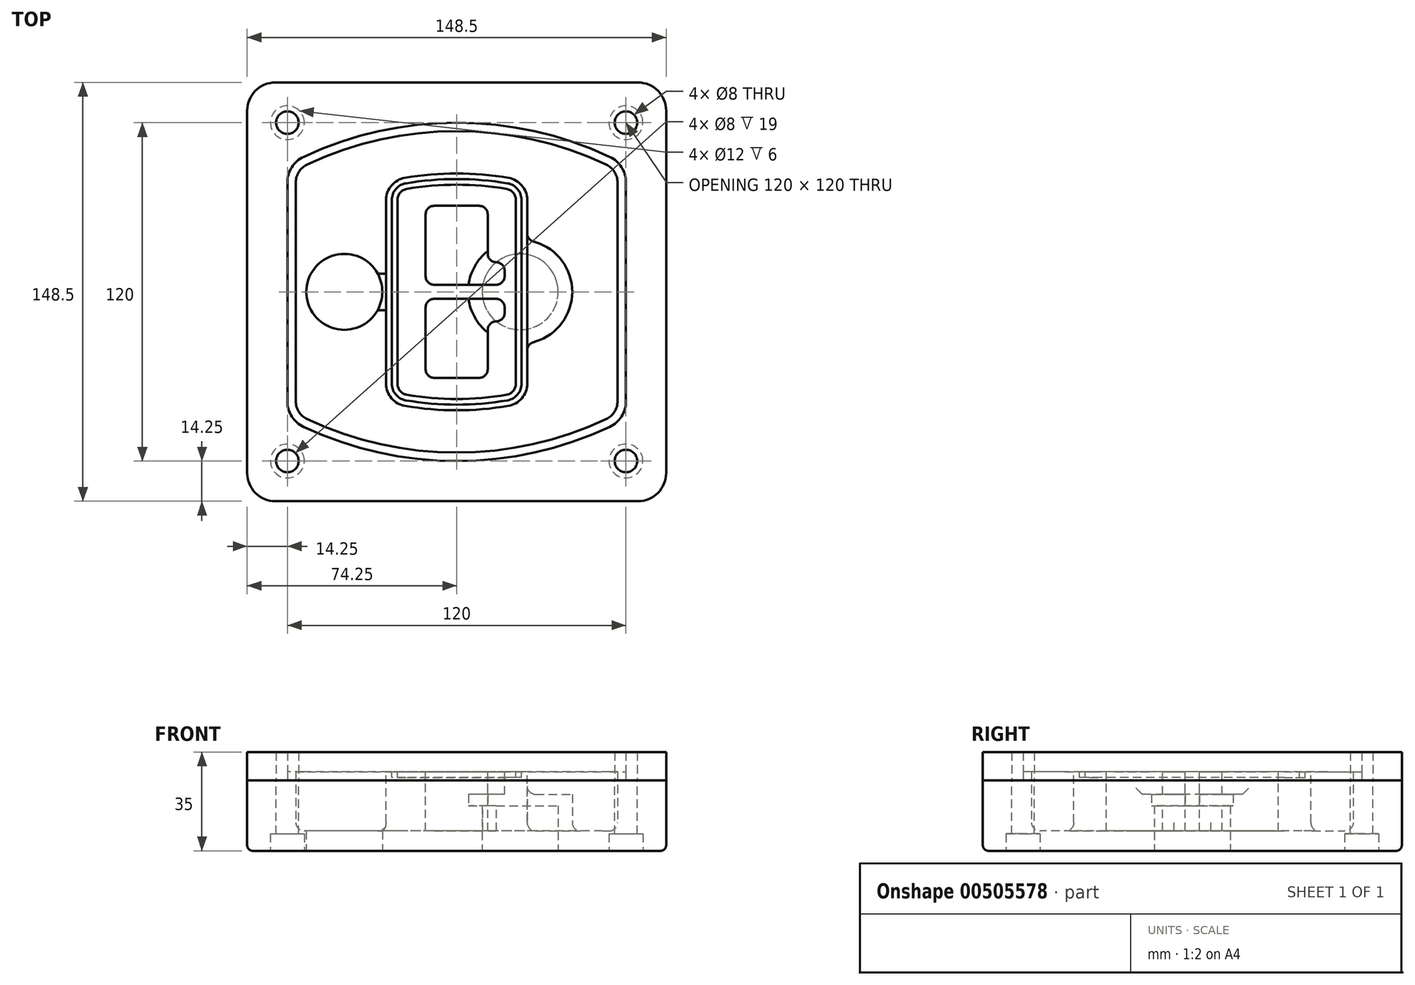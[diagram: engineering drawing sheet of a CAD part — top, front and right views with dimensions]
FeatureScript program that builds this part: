
annotation { "Feature Type Name" : "Feature", "Feature Type Description" : "" }
export const myFeature = defineFeature(function(context is Context, id is Id, definition is map)
    precondition{}
    {
        {
            var Q0;
            Q0=qCreatedBy(makeId("Top.planeOp"),FACE);
            var sketch = newSketch(context, id + "F0", { "sketchPlane" : qUnion([Q0])});
            skPoint(sketch, "E0.rect.middle", {"position": v(0, 0) * mm});
            skLineSegment(sketch, "E1.bottom", {"start": v(-64.25, -74.25) * mm, "end": v(64.25, -74.25) * mm});
            skLineSegment(sketch, "E1.top", {"start": v(-64.25, 74.25) * mm, "end": v(64.25, 74.25) * mm});
            skLineSegment(sketch, "E1.left", {"start": v(-74.25, -64.25) * mm, "end": v(-74.25, 64.25) * mm});
            skLineSegment(sketch, "E1.right", {"start": v(74.25, -64.25) * mm, "end": v(74.25, 64.25) * mm});
            skLineSegment(sketch, "E2", {"start": v(-74.25, 74.25) * mm, "end": v(74.25, -74.25) * mm, "construction": true});
            skLineSegment(sketch, "E3", {"start": v(74.25, 74.25) * mm, "end": v(-74.25, -74.25) * mm, "construction": true});
            skCircle(sketch, "E4", {"center": v(-60, 60) * mm, "radius": 4 * mm});
            skCircle(sketch, "E5", {"center": v(60, 60) * mm, "radius": 4 * mm});
            skCircle(sketch, "E6", {"center": v(60, -60) * mm, "radius": 4 * mm});
            skCircle(sketch, "E7", {"center": v(-60, -60) * mm, "radius": 4 * mm});
            skLineSegment(sketch, "E8", {"start": v(-60, 60) * mm, "end": v(60, 60) * mm, "construction": true});
            skLineSegment(sketch, "E9", {"start": v(60, 60) * mm, "end": v(60, -60) * mm, "construction": true});
            skLineSegment(sketch, "E10", {"start": v(60, -60) * mm, "end": v(-60, -60) * mm, "construction": true});
            skLineSegment(sketch, "E11", {"start": v(-60, -60) * mm, "end": v(-60, 60) * mm, "construction": true});
            skLineSegment(sketch, "E12", {"start": v(-60, 38.83) * mm, "end": v(-60, -38.83) * mm});
            skLineSegment(sketch, "E13", {"start": v(60, 38.83) * mm, "end": v(60, -38.83) * mm});
            skArc(sketch, "E14", {"start": v(54.26, 47.88) * mm, "mid": v(0, 60) * mm, "end": v(-54.26, 47.88) * mm});
            skArc(sketch, "E15", {"start": v(-54.26, -47.88) * mm, "mid": v(0, -60) * mm, "end": v(54.26, -47.88) * mm});
            skLineSegment(sketch, "E16", {"start": v(-60, 0) * mm, "end": v(60, 0) * mm, "construction": true});
            skPoint(sketch, "E17.visualSharp", {"position": v(-60, -45) * mm});
            skArc(sketch, "E17.filletArc", {"start": v(-60, -38.83) * mm, "mid": v(-58.44, -44.2) * mm, "end": v(-54.26, -47.88) * mm});
            skPoint(sketch, "E18.visualSharp", {"position": v(-60, 45) * mm});
            skArc(sketch, "E18.filletArc", {"start": v(-54.26, 47.88) * mm, "mid": v(-58.44, 44.2) * mm, "end": v(-60, 38.83) * mm});
            skPoint(sketch, "E19.visualSharp", {"position": v(60, 45) * mm});
            skArc(sketch, "E19.filletArc", {"start": v(60, 38.83) * mm, "mid": v(58.44, 44.2) * mm, "end": v(54.26, 47.88) * mm});
            skPoint(sketch, "E20.visualSharp", {"position": v(60, -45) * mm});
            skArc(sketch, "E20.filletArc", {"start": v(54.26, -47.88) * mm, "mid": v(58.44, -44.2) * mm, "end": v(60, -38.83) * mm});
            skPoint(sketch, "E21.visualSharp", {"position": v(-74.25, 74.25) * mm});
            skArc(sketch, "E21.filletArc", {"start": v(-64.25, 74.25) * mm, "mid": v(-71.32, 71.32) * mm, "end": v(-74.25, 64.25) * mm});
            skPoint(sketch, "E22.visualSharp", {"position": v(74.25, 74.25) * mm});
            skArc(sketch, "E22.filletArc", {"start": v(74.25, 64.25) * mm, "mid": v(71.32, 71.32) * mm, "end": v(64.25, 74.25) * mm});
            skPoint(sketch, "E23.visualSharp", {"position": v(74.25, -74.25) * mm});
            skArc(sketch, "E23.filletArc", {"start": v(64.25, -74.25) * mm, "mid": v(71.32, -71.32) * mm, "end": v(74.25, -64.25) * mm});
            skPoint(sketch, "E24.visualSharp", {"position": v(-74.25, -74.25) * mm});
            skArc(sketch, "E24.filletArc", {"start": v(-74.25, -64.25) * mm, "mid": v(-71.32, -71.32) * mm, "end": v(-64.25, -74.25) * mm});
            skArc(sketch, "E25.0", {"start": v(57, 38.83) * mm, "mid": v(55.9, 42.58) * mm, "end": v(52.98, 45.17) * mm});
            skLineSegment(sketch, "E25.1", {"start": v(57, 38.83) * mm, "end": v(57, -38.83) * mm});
            skArc(sketch, "E25.2", {"start": v(52.98, -45.17) * mm, "mid": v(55.9, -42.58) * mm, "end": v(57, -38.83) * mm});
            skArc(sketch, "E25.3", {"start": v(-52.98, -45.17) * mm, "mid": v(0, -57) * mm, "end": v(52.98, -45.17) * mm});
            skArc(sketch, "E25.4", {"start": v(-57, -38.83) * mm, "mid": v(-55.9, -42.58) * mm, "end": v(-52.98, -45.17) * mm});
            skArc(sketch, "E25.5", {"start": v(52.98, 45.17) * mm, "mid": v(0, 57) * mm, "end": v(-52.98, 45.17) * mm});
            skLineSegment(sketch, "E25.6", {"start": v(-57, 38.83) * mm, "end": v(-57, -38.83) * mm});
            skArc(sketch, "E25.7", {"start": v(-52.98, 45.17) * mm, "mid": v(-55.9, 42.58) * mm, "end": v(-57, 38.83) * mm});
            skArc(sketch, "E26.0", {"start": v(-55.96, 51.5) * mm, "mid": v(-61.82, 46.33) * mm, "end": v(-64, 38.83) * mm});
            skArc(sketch, "E26.1", {"start": v(55.96, 51.5) * mm, "mid": v(0, 64) * mm, "end": v(-55.96, 51.5) * mm});
            skArc(sketch, "E26.2", {"start": v(64, 38.83) * mm, "mid": v(61.82, 46.33) * mm, "end": v(55.96, 51.5) * mm});
            skLineSegment(sketch, "E26.3", {"start": v(64, 38.83) * mm, "end": v(64, -38.83) * mm});
            skArc(sketch, "E26.4", {"start": v(55.96, -51.5) * mm, "mid": v(61.82, -46.33) * mm, "end": v(64, -38.83) * mm});
            skLineSegment(sketch, "E26.5", {"start": v(-64, 38.83) * mm, "end": v(-64, -38.83) * mm});
            skArc(sketch, "E26.6", {"start": v(-55.96, -51.5) * mm, "mid": v(0, -64) * mm, "end": v(55.96, -51.5) * mm});
            skArc(sketch, "E26.7", {"start": v(-64, -38.83) * mm, "mid": v(-61.82, -46.33) * mm, "end": v(-55.96, -51.5) * mm});
            skSolve(sketch);
        }
        {
            var Q0;
            Q0=makeQuery(id+"F0.imprint","IMPRINT",FACE,{"disambiguationData":[TD([[makeQuery(id+"F0.imprint","IMPRINT",EDGE,{"derivedFrom":sQuery(id+"F0.wireOp",EDGE,"E1.bottom")}),1.0]])]});
            var Q1;
            Q1=makeQuery(id+"F0.imprint","IMPRINT",FACE,{"disambiguationData":[TD([[makeQuery(id+"F0.imprint","IMPRINT",EDGE,{"derivedFrom":sQuery(id+"F0.wireOp",EDGE,"E12")}),1.0]])]});
            var Q2;
            Q2=makeQuery(id+"F0.imprint","IMPRINT",FACE,{"disambiguationData":[TD([[makeQuery(id+"F0.imprint","IMPRINT",EDGE,{"derivedFrom":sQuery(id+"F0.wireOp",EDGE,"E25.0")}),1.0]])]});
            var Q3;
            Q3=makeQuery(id+"F0.imprint","IMPRINT",FACE,{"disambiguationData":[TD([[makeQuery(id+"F0.imprint","IMPRINT",EDGE,{"derivedFrom":sQuery(id+"F0.wireOp",EDGE,"E12")}),-1.0]])]});
            extrude(context, id + "F1", {"entities" : qUnion([Q0, Q1, Q2, Q3]), "oppositeDirection" : true, "depth" : 25 * mm});
        }
        {
            var Q0;
            Q0=makeQuery(id+"F0.imprint","IMPRINT",FACE,{"disambiguationData":[TD([[makeQuery(id+"F0.imprint","IMPRINT",EDGE,{"derivedFrom":sQuery(id+"F0.wireOp",EDGE,"E12")}),1.0]])]});
            extrude(context, id + "F2", {"entities" : qUnion([Q0]), "operationType" : NewBodyOperationType.ADD, "depth" : 3 * mm});
        }
        {
            var Q0;
            Q0=makeQuery(id+"F0.imprint","IMPRINT",FACE,{"disambiguationData":[TD([[makeQuery(id+"F0.imprint","IMPRINT",EDGE,{"derivedFrom":sQuery(id+"F0.wireOp",EDGE,"E25.0")}),1.0]])]});
            extrude(context, id + "F3", {"entities" : qUnion([Q0]), "operationType" : NewBodyOperationType.REMOVE, "oppositeDirection" : true, "depth" : 18 * mm});
        }
        {
            var Q0;
            Q0=makeQuery(id+"F2.opExtrude","CAP_FACE",FACE,{"disambiguationData":[OSD([sQuery(id+"F0.wireOp",EDGE,"E12"),sQuery(id+"F0.wireOp",EDGE,"E13"),sQuery(id+"F0.wireOp",EDGE,"E14"),sQuery(id+"F0.wireOp",EDGE,"E15"),sQuery(id+"F0.wireOp",EDGE,"E17.filletArc"),sQuery(id+"F0.wireOp",EDGE,"E18.filletArc"),sQuery(id+"F0.wireOp",EDGE,"E19.filletArc"),sQuery(id+"F0.wireOp",EDGE,"E20.filletArc"),sQuery(id+"F0.wireOp",EDGE,"E25.0"),sQuery(id+"F0.wireOp",EDGE,"E25.1"),sQuery(id+"F0.wireOp",EDGE,"E25.2"),sQuery(id+"F0.wireOp",EDGE,"E25.3"),sQuery(id+"F0.wireOp",EDGE,"E25.4"),sQuery(id+"F0.wireOp",EDGE,"E25.5"),sQuery(id+"F0.wireOp",EDGE,"E25.6"),sQuery(id+"F0.wireOp",EDGE,"E25.7")])],"isStart":false});
            var sketch = newSketch(context, id + "F4", { "sketchPlane" : qUnion([Q0])});
            skArc(sketch, "E27.0", {"start": v(-18.34, -40.45) * mm, "mid": v(0, -42) * mm, "end": v(18.34, -40.45) * mm});
            skArc(sketch, "E28.0", {"start": v(18.34, 40.45) * mm, "mid": v(0, 42) * mm, "end": v(-18.34, 40.45) * mm});
            skLineSegment(sketch, "E29", {"start": v(-25, 32.57) * mm, "end": v(-25, -32.57) * mm});
            skLineSegment(sketch, "E30", {"start": v(25, 32.57) * mm, "end": v(25, -32.57) * mm});
            skLineSegment(sketch, "E31", {"start": v(-25, 39.1) * mm, "end": v(25, 39.1) * mm, "construction": true});
            skLineSegment(sketch, "E32", {"start": v(-25, -39.1) * mm, "end": v(25, -39.1) * mm, "construction": true});
            skPoint(sketch, "E33.visualSharp", {"position": v(-25, 39.1) * mm});
            skArc(sketch, "E33.filletArc", {"start": v(-18.34, 40.45) * mm, "mid": v(-23.11, 37.73) * mm, "end": v(-25, 32.57) * mm});
            skPoint(sketch, "E34.visualSharp", {"position": v(25, 39.1) * mm});
            skArc(sketch, "E34.filletArc", {"start": v(25, 32.57) * mm, "mid": v(23.11, 37.73) * mm, "end": v(18.34, 40.45) * mm});
            skPoint(sketch, "E35.visualSharp", {"position": v(25, -39.1) * mm});
            skArc(sketch, "E35.filletArc", {"start": v(18.34, -40.45) * mm, "mid": v(23.11, -37.73) * mm, "end": v(25, -32.57) * mm});
            skPoint(sketch, "E36.visualSharp", {"position": v(-25, -39.1) * mm});
            skArc(sketch, "E36.filletArc", {"start": v(-25, -32.57) * mm, "mid": v(-23.11, -37.73) * mm, "end": v(-18.34, -40.45) * mm});
            skArc(sketch, "E37.0", {"start": v(52.98, 45.17) * mm, "mid": v(0, 57) * mm, "end": v(-52.98, 45.17) * mm});
            skArc(sketch, "E37.1", {"start": v(-52.98, 45.17) * mm, "mid": v(-55.9, 42.58) * mm, "end": v(-57, 38.83) * mm});
            skLineSegment(sketch, "E37.2", {"start": v(-57, 38.83) * mm, "end": v(-57, -38.83) * mm});
            skArc(sketch, "E37.3", {"start": v(-57, -38.83) * mm, "mid": v(-55.9, -42.58) * mm, "end": v(-52.98, -45.17) * mm});
            skArc(sketch, "E37.4", {"start": v(-52.98, -45.17) * mm, "mid": v(0, -57) * mm, "end": v(52.98, -45.17) * mm});
            skArc(sketch, "E37.5", {"start": v(52.98, -45.17) * mm, "mid": v(55.9, -42.58) * mm, "end": v(57, -38.83) * mm});
            skLineSegment(sketch, "E37.6", {"start": v(57, 38.83) * mm, "end": v(57, -38.83) * mm});
            skArc(sketch, "E37.7", {"start": v(57, 38.83) * mm, "mid": v(55.9, 42.58) * mm, "end": v(52.98, 45.17) * mm});
            skLineSegment(sketch, "E38.0", {"start": v(23, 32.57) * mm, "end": v(23, -32.57) * mm});
            skArc(sketch, "E38.1", {"start": v(18, -38.48) * mm, "mid": v(21.58, -36.44) * mm, "end": v(23, -32.57) * mm});
            skArc(sketch, "E38.2", {"start": v(-18, -38.48) * mm, "mid": v(0, -40) * mm, "end": v(18, -38.48) * mm});
            skArc(sketch, "E38.3", {"start": v(-23, -32.57) * mm, "mid": v(-21.58, -36.44) * mm, "end": v(-18, -38.48) * mm});
            skLineSegment(sketch, "E38.4", {"start": v(-23, 32.57) * mm, "end": v(-23, -32.57) * mm});
            skArc(sketch, "E38.5", {"start": v(23, 32.57) * mm, "mid": v(21.58, 36.44) * mm, "end": v(18, 38.48) * mm});
            skArc(sketch, "E38.6", {"start": v(-18, 38.48) * mm, "mid": v(-21.58, 36.44) * mm, "end": v(-23, 32.57) * mm});
            skArc(sketch, "E38.7", {"start": v(18, 38.48) * mm, "mid": v(0, 40) * mm, "end": v(-18, 38.48) * mm});
            skArc(sketch, "E39.0", {"start": v(21, 32.57) * mm, "mid": v(20.06, 35.15) * mm, "end": v(17.67, 36.5) * mm});
            skLineSegment(sketch, "E39.1", {"start": v(21, 32.57) * mm, "end": v(21, -32.57) * mm});
            skArc(sketch, "E39.2", {"start": v(17.67, -36.5) * mm, "mid": v(20.06, -35.15) * mm, "end": v(21, -32.57) * mm});
            skArc(sketch, "E39.3", {"start": v(-17.67, -36.5) * mm, "mid": v(0, -38) * mm, "end": v(17.67, -36.5) * mm});
            skArc(sketch, "E39.4", {"start": v(-21, -32.57) * mm, "mid": v(-20.06, -35.15) * mm, "end": v(-17.67, -36.5) * mm});
            skArc(sketch, "E39.5", {"start": v(17.67, 36.5) * mm, "mid": v(0, 38) * mm, "end": v(-17.67, 36.5) * mm});
            skLineSegment(sketch, "E39.6", {"start": v(-21, 32.57) * mm, "end": v(-21, -32.57) * mm});
            skArc(sketch, "E39.7", {"start": v(-17.67, 36.5) * mm, "mid": v(-20.06, 35.15) * mm, "end": v(-21, 32.57) * mm});
            skLineSegment(sketch, "E40", {"start": v(-25, 0) * mm, "end": v(25, 0) * mm, "construction": true});
            skLineSegment(sketch, "E41", {"start": v(-11, 5.5) * mm, "end": v(-11, 27.5) * mm});
            skLineSegment(sketch, "E42", {"start": v(-8, 30.5) * mm, "end": v(8, 30.5) * mm});
            skLineSegment(sketch, "E43", {"start": v(11, 27.5) * mm, "end": v(11, 13.5) * mm});
            skLineSegment(sketch, "E44", {"start": v(14, 10.5) * mm, "end": v(14, 10.5) * mm});
            skLineSegment(sketch, "E45", {"start": v(17, 7.5) * mm, "end": v(17, 5.5) * mm});
            skLineSegment(sketch, "E46", {"start": v(14, 2.5) * mm, "end": v(-8, 2.5) * mm});
            skPoint(sketch, "E47.visualSharp", {"position": v(-11, 30.5) * mm});
            skArc(sketch, "E47.filletArc", {"start": v(-8, 30.5) * mm, "mid": v(-10.12, 29.62) * mm, "end": v(-11, 27.5) * mm});
            skPoint(sketch, "E48.visualSharp", {"position": v(11, 30.5) * mm});
            skArc(sketch, "E48.filletArc", {"start": v(11, 27.5) * mm, "mid": v(10.12, 29.62) * mm, "end": v(8, 30.5) * mm});
            skPoint(sketch, "E49.visualSharp", {"position": v(11, 10.5) * mm});
            skArc(sketch, "E49.filletArc", {"start": v(11, 13.5) * mm, "mid": v(11.88, 11.38) * mm, "end": v(14, 10.5) * mm});
            skPoint(sketch, "E50.visualSharp", {"position": v(17, 10.5) * mm});
            skArc(sketch, "E50.filletArc", {"start": v(17, 7.5) * mm, "mid": v(16.12, 9.62) * mm, "end": v(14, 10.5) * mm});
            skPoint(sketch, "E51.visualSharp", {"position": v(17, 2.5) * mm});
            skArc(sketch, "E51.filletArc", {"start": v(14, 2.5) * mm, "mid": v(16.12, 3.38) * mm, "end": v(17, 5.5) * mm});
            skPoint(sketch, "E52.visualSharp", {"position": v(-11, 2.5) * mm});
            skArc(sketch, "E52.filletArc", {"start": v(-11, 5.5) * mm, "mid": v(-10.12, 3.38) * mm, "end": v(-8, 2.5) * mm});
            skLineSegment(sketch, "E53.0.MirrorCS", {"start": v(14, -2.5) * mm, "end": v(-8, -2.5) * mm});
            skArc(sketch, "E54.0.MirrorCS", {"start": v(-11, -5.5) * mm, "mid": v(-10.12, -3.38) * mm, "end": v(-8, -2.5) * mm});
            skLineSegment(sketch, "E55.0.MirrorCS", {"start": v(-11, -5.5) * mm, "end": v(-11, -27.5) * mm});
            skArc(sketch, "E56.0.MirrorCS", {"start": v(-8, -30.5) * mm, "mid": v(-10.12, -29.62) * mm, "end": v(-11, -27.5) * mm});
            skLineSegment(sketch, "E57.0.MirrorCS", {"start": v(-8, -30.5) * mm, "end": v(8, -30.5) * mm});
            skArc(sketch, "E58.0.MirrorCS", {"start": v(11, -27.5) * mm, "mid": v(10.12, -29.62) * mm, "end": v(8, -30.5) * mm});
            skLineSegment(sketch, "E59.0.MirrorCS", {"start": v(11, -27.5) * mm, "end": v(11, -13.5) * mm});
            skArc(sketch, "E60.0.MirrorCS", {"start": v(11, -13.5) * mm, "mid": v(11.88, -11.38) * mm, "end": v(14, -10.5) * mm});
            skArc(sketch, "E61.0.MirrorCS", {"start": v(17, -7.5) * mm, "mid": v(16.12, -9.62) * mm, "end": v(14, -10.5) * mm});
            skLineSegment(sketch, "E62.0.MirrorCS", {"start": v(17, -7.5) * mm, "end": v(17, -5.5) * mm});
            skArc(sketch, "E63.0.MirrorCS", {"start": v(14, -2.5) * mm, "mid": v(16.12, -3.38) * mm, "end": v(17, -5.5) * mm});
            skSolve(sketch);
        }
        {
            var Q0;
            Q0=makeQuery(id+"F4.imprint","IMPRINT",FACE,{"disambiguationData":[TD([[makeQuery(id+"F4.imprint","IMPRINT",EDGE,{"derivedFrom":sQuery(id+"F4.wireOp",EDGE,"E27.0")}),1.0]])]});
            var Q1;
            Q1=makeQuery(id+"F4.imprint","IMPRINT",FACE,{"disambiguationData":[TD([[makeQuery(id+"F4.imprint","IMPRINT",EDGE,{"derivedFrom":sQuery(id+"F4.wireOp",EDGE,"E38.0")}),-1.0]])]});
            var Q2;
            Q2=makeQuery(id+"F4.imprint","IMPRINT",FACE,{"disambiguationData":[TD([[makeQuery(id+"F4.imprint","IMPRINT",EDGE,{"derivedFrom":sQuery(id+"F4.wireOp",EDGE,"E39.0")}),1.0]])]});
            extrude(context, id + "F5", {"entities" : qUnion([Q0, Q1, Q2]), "operationType" : NewBodyOperationType.ADD, "endBound" : BoundingType.UP_TO_NEXT, "oppositeDirection" : true, "depth" : 25 * mm});
        }
        {
            var Q0;
            Q0=makeQuery(id+"F4.imprint","IMPRINT",FACE,{"disambiguationData":[TD([[makeQuery(id+"F4.imprint","IMPRINT",EDGE,{"derivedFrom":sQuery(id+"F4.wireOp",EDGE,"E38.0")}),-1.0]])]});
            extrude(context, id + "F6", {"entities" : qUnion([Q0]), "operationType" : NewBodyOperationType.REMOVE, "oppositeDirection" : true, "depth" : 2 * mm});
        }
        {
            var Q0;
            Q0=makeQuery(id+"F1.opExtrude","CAP_FACE",FACE,{"disambiguationData":[OSD([sQuery(id+"F0.wireOp",EDGE,"E1.bottom"),sQuery(id+"F0.wireOp",EDGE,"E1.top"),sQuery(id+"F0.wireOp",EDGE,"E1.left"),sQuery(id+"F0.wireOp",EDGE,"E1.right"),sQuery(id+"F0.wireOp",EDGE,"E4"),sQuery(id+"F0.wireOp",EDGE,"E5"),sQuery(id+"F0.wireOp",EDGE,"E6"),sQuery(id+"F0.wireOp",EDGE,"E7"),sQuery(id+"F0.wireOp",EDGE,"E21.filletArc"),sQuery(id+"F0.wireOp",EDGE,"E22.filletArc"),sQuery(id+"F0.wireOp",EDGE,"E23.filletArc"),sQuery(id+"F0.wireOp",EDGE,"E24.filletArc")])],"isStart":false});
            var sketch = newSketch(context, id + "F7", { "sketchPlane" : qUnion([Q0])});
            skCircle(sketch, "E64", {"center": v(22.5, 0) * mm, "radius": 13.47 * mm});
            skCircle(sketch, "E65", {"center": v(-39.81, 0) * mm, "radius": 13.47 * mm});
            skLineSegment(sketch, "E66", {"start": v(74.25, 0) * mm, "end": v(-74.25, 0) * mm});
            skCircle(sketch, "E67", {"center": v(22.5, 0) * mm, "radius": 18.47 * mm});
            skCircle(sketch, "E68", {"center": v(60, -60) * mm, "radius": 6 * mm});
            skCircle(sketch, "E69", {"center": v(-60, -60) * mm, "radius": 6 * mm});
            skCircle(sketch, "E70", {"center": v(-60, 60) * mm, "radius": 6 * mm});
            skCircle(sketch, "E71", {"center": v(60, 60) * mm, "radius": 6 * mm});
            skSolve(sketch);
        }
        {
            var Q0;
            {var subQ1=sQuery(id+"F7.wireOp",EDGE,"E66");var subQ4=sQuery(id+"F7.wireOp",EDGE,"E64");var subQ6=makeQuery(id+"F7.imprint","INTERSECT",VERTEX,{"disambiguationData":[OD(0.0)],"derivedFrom":[subQ4,subQ1]});Q0=makeQuery(id+"F7.imprint","IMPRINT",FACE,{"disambiguationData":[TD([[makeQuery(id+"F7.imprint","IMPRINT",EDGE,{"disambiguationData":[TD([[subQ6,-1.0]])],"derivedFrom":subQ4}),-1.0]])]});}
            var Q1;
            {var subQ0=sQuery(id+"F7.wireOp",EDGE,"E66");var subQ1=sQuery(id+"F7.wireOp",EDGE,"E64");var subQ3=makeQuery(id+"F7.imprint","INTERSECT",VERTEX,{"disambiguationData":[OD(0.0)],"derivedFrom":[subQ1,subQ0]});Q1=makeQuery(id+"F7.imprint","IMPRINT",FACE,{"disambiguationData":[TD([[makeQuery(id+"F7.imprint","IMPRINT",EDGE,{"disambiguationData":[TD([[subQ3,-1.0]])],"derivedFrom":subQ1}),1.0]])]});}
            var Q2;
            {var subQ0=sQuery(id+"F7.wireOp",EDGE,"E66");var subQ1=sQuery(id+"F7.wireOp",EDGE,"E64");var subQ3=makeQuery(id+"F7.imprint","INTERSECT",VERTEX,{"disambiguationData":[OD(0.0)],"derivedFrom":[subQ1,subQ0]});Q2=makeQuery(id+"F7.imprint","IMPRINT",FACE,{"disambiguationData":[TD([[makeQuery(id+"F7.imprint","IMPRINT",EDGE,{"disambiguationData":[TD([[subQ3,1.0]])],"derivedFrom":subQ1}),1.0]])]});}
            var Q3;
            {var subQ1=sQuery(id+"F7.wireOp",EDGE,"E66");var subQ4=sQuery(id+"F7.wireOp",EDGE,"E64");var subQ6=makeQuery(id+"F7.imprint","INTERSECT",VERTEX,{"disambiguationData":[OD(0.0)],"derivedFrom":[subQ4,subQ1]});Q3=makeQuery(id+"F7.imprint","IMPRINT",FACE,{"disambiguationData":[TD([[makeQuery(id+"F7.imprint","IMPRINT",EDGE,{"disambiguationData":[TD([[subQ6,1.0]])],"derivedFrom":subQ4}),-1.0]])]});}
            extrude(context, id + "F8", {"entities" : qUnion([Q0, Q1, Q2, Q3]), "operationType" : NewBodyOperationType.ADD, "oppositeDirection" : true, "depth" : 20 * mm});
        }
        {
            var Q0;
            {var subQ0=sQuery(id+"F7.wireOp",EDGE,"E66");var subQ1=sQuery(id+"F7.wireOp",EDGE,"E64");var subQ3=makeQuery(id+"F7.imprint","INTERSECT",VERTEX,{"disambiguationData":[OD(0.0)],"derivedFrom":[subQ1,subQ0]});Q0=makeQuery(id+"F7.imprint","IMPRINT",FACE,{"disambiguationData":[TD([[makeQuery(id+"F7.imprint","IMPRINT",EDGE,{"disambiguationData":[TD([[subQ3,-1.0]])],"derivedFrom":subQ1}),1.0]])]});}
            var Q1;
            {var subQ0=sQuery(id+"F7.wireOp",EDGE,"E66");var subQ1=sQuery(id+"F7.wireOp",EDGE,"E64");var subQ3=makeQuery(id+"F7.imprint","INTERSECT",VERTEX,{"disambiguationData":[OD(0.0)],"derivedFrom":[subQ1,subQ0]});Q1=makeQuery(id+"F7.imprint","IMPRINT",FACE,{"disambiguationData":[TD([[makeQuery(id+"F7.imprint","IMPRINT",EDGE,{"disambiguationData":[TD([[subQ3,1.0]])],"derivedFrom":subQ1}),1.0]])]});}
            extrude(context, id + "F9", {"entities" : qUnion([Q0, Q1]), "operationType" : NewBodyOperationType.REMOVE, "oppositeDirection" : true, "depth" : 16 * mm});
        }
        {
            var Q0;
            {var subQ0=sQuery(id+"F7.wireOp",EDGE,"E66");var subQ1=sQuery(id+"F7.wireOp",EDGE,"E65");var subQ3=makeQuery(id+"F7.imprint","INTERSECT",VERTEX,{"disambiguationData":[OD(0.0)],"derivedFrom":[subQ1,subQ0]});Q0=makeQuery(id+"F7.imprint","IMPRINT",FACE,{"disambiguationData":[TD([[makeQuery(id+"F7.imprint","IMPRINT",EDGE,{"disambiguationData":[TD([[subQ3,-1.0]])],"derivedFrom":subQ1}),1.0]])]});}
            var Q1;
            {var subQ0=sQuery(id+"F7.wireOp",EDGE,"E66");var subQ1=sQuery(id+"F7.wireOp",EDGE,"E65");var subQ3=makeQuery(id+"F7.imprint","INTERSECT",VERTEX,{"disambiguationData":[OD(0.0)],"derivedFrom":[subQ1,subQ0]});Q1=makeQuery(id+"F7.imprint","IMPRINT",FACE,{"disambiguationData":[TD([[makeQuery(id+"F7.imprint","IMPRINT",EDGE,{"disambiguationData":[TD([[subQ3,1.0]])],"derivedFrom":subQ1}),1.0]])]});}
            extrude(context, id + "F10", {"entities" : qUnion([Q0, Q1]), "operationType" : NewBodyOperationType.REMOVE, "oppositeDirection" : true, "depth" : 25 * mm});
        }
        {
            var Q0;
            Q0=makeQuery(id+"F7.imprint","IMPRINT",FACE,{"disambiguationData":[TD([[makeQuery(id+"F7.imprint","IMPRINT",EDGE,{"derivedFrom":sQuery(id+"F7.wireOp",EDGE,"E68")}),1.0]])]});
            var Q1;
            Q1=makeQuery(id+"F7.imprint","IMPRINT",FACE,{"disambiguationData":[TD([[makeQuery(id+"F7.imprint","IMPRINT",EDGE,{"derivedFrom":makeQuery(id+"F1.opExtrude","CAP_EDGE",EDGE,{"disambiguationData":[OSD([sQuery(id+"F0.wireOp",EDGE,"E5")])],"isStart":false})}),-1.0]])]});
            var Q2;
            Q2=makeQuery(id+"F7.imprint","IMPRINT",FACE,{"disambiguationData":[TD([[makeQuery(id+"F7.imprint","IMPRINT",EDGE,{"derivedFrom":sQuery(id+"F7.wireOp",EDGE,"E69")}),1.0]])]});
            var Q3;
            Q3=makeQuery(id+"F7.imprint","IMPRINT",FACE,{"disambiguationData":[TD([[makeQuery(id+"F7.imprint","IMPRINT",EDGE,{"derivedFrom":makeQuery(id+"F1.opExtrude","CAP_EDGE",EDGE,{"disambiguationData":[OSD([sQuery(id+"F0.wireOp",EDGE,"E4")])],"isStart":false})}),-1.0]])]});
            var Q4;
            Q4=makeQuery(id+"F7.imprint","IMPRINT",FACE,{"disambiguationData":[TD([[makeQuery(id+"F7.imprint","IMPRINT",EDGE,{"derivedFrom":sQuery(id+"F7.wireOp",EDGE,"E70")}),1.0]])]});
            var Q5;
            Q5=makeQuery(id+"F7.imprint","IMPRINT",FACE,{"disambiguationData":[TD([[makeQuery(id+"F7.imprint","IMPRINT",EDGE,{"derivedFrom":makeQuery(id+"F1.opExtrude","CAP_EDGE",EDGE,{"disambiguationData":[OSD([sQuery(id+"F0.wireOp",EDGE,"E7")])],"isStart":false})}),-1.0]])]});
            var Q6;
            Q6=makeQuery(id+"F7.imprint","IMPRINT",FACE,{"disambiguationData":[TD([[makeQuery(id+"F7.imprint","IMPRINT",EDGE,{"derivedFrom":sQuery(id+"F7.wireOp",EDGE,"E71")}),1.0]])]});
            var Q7;
            Q7=makeQuery(id+"F7.imprint","IMPRINT",FACE,{"disambiguationData":[TD([[makeQuery(id+"F7.imprint","IMPRINT",EDGE,{"derivedFrom":makeQuery(id+"F1.opExtrude","CAP_EDGE",EDGE,{"disambiguationData":[OSD([sQuery(id+"F0.wireOp",EDGE,"E6")])],"isStart":false})}),-1.0]])]});
            extrude(context, id + "F11", {"entities" : qUnion([Q0, Q1, Q2, Q3, Q4, Q5, Q6, Q7]), "operationType" : NewBodyOperationType.REMOVE, "oppositeDirection" : true, "depth" : 6 * mm});
        }
        {
            var Q0;
            Q0=makeQuery(id+"F9.boolean.opBoolean","COPY",FACE,{"derivedFrom":makeQuery(id+"F9.opExtrude","CAP_FACE",FACE,{"disambiguationData":[OSD([sQuery(id+"F7.wireOp",EDGE,"E64")])],"isStart":false})});
            var sketch = newSketch(context, id + "F12", { "sketchPlane" : qUnion([Q0])});
            skArc(sketch, "E72.0", {"start": v(11, 14.45) * mm, "mid": v(6.45, 9.13) * mm, "end": v(4.2, 2.5) * mm});
            skArc(sketch, "E72.1", {"start": v(4.2, -2.5) * mm, "mid": v(6.45, -9.13) * mm, "end": v(11, -14.45) * mm});
            skLineSegment(sketch, "E73", {"start": v(4.2, -2.5) * mm, "end": v(14, -2.5) * mm});
            skLineSegment(sketch, "E74.0", {"start": v(14, 2.5) * mm, "end": v(4.2, 2.5) * mm});
            skArc(sketch, "E74.1", {"start": v(14, 2.5) * mm, "mid": v(16.12, 3.38) * mm, "end": v(17, 5.5) * mm});
            skLineSegment(sketch, "E74.2", {"start": v(17, 7.5) * mm, "end": v(17, 5.5) * mm});
            skArc(sketch, "E74.3", {"start": v(17, 7.5) * mm, "mid": v(16.12, 9.62) * mm, "end": v(14, 10.5) * mm});
            skArc(sketch, "E74.4", {"start": v(11, 13.5) * mm, "mid": v(11.88, 11.38) * mm, "end": v(14, 10.5) * mm});
            skLineSegment(sketch, "E74.5", {"start": v(11, 14.45) * mm, "end": v(11, 13.5) * mm});
            skLineSegment(sketch, "E74.7", {"start": v(14, -2.5) * mm, "end": v(4.2, -2.5) * mm});
            skArc(sketch, "E74.8", {"start": v(14, -2.5) * mm, "mid": v(16.12, -3.38) * mm, "end": v(17, -5.5) * mm});
            skLineSegment(sketch, "E74.9", {"start": v(17, -7.5) * mm, "end": v(17, -5.5) * mm});
            skArc(sketch, "E74.10", {"start": v(17, -7.5) * mm, "mid": v(16.12, -9.62) * mm, "end": v(14, -10.5) * mm});
            skArc(sketch, "E74.11", {"start": v(11, -13.5) * mm, "mid": v(11.88, -11.38) * mm, "end": v(14, -10.5) * mm});
            skLineSegment(sketch, "E74.12", {"start": v(11, -14.45) * mm, "end": v(11, -13.5) * mm});
            skPoint(sketch, "E75.orphan", {"position": v(11, -27.5) * mm});
            skPoint(sketch, "E76.orphan", {"position": v(-8, -2.5) * mm});
            skPoint(sketch, "E77.orphan", {"position": v(-8, 2.5) * mm});
            skPoint(sketch, "E78.orphan", {"position": v(11, 27.5) * mm});
            skSolve(sketch);
        }
        {
            var Q0;
            {var subQ7=sQuery(id+"F12.wireOp",EDGE,"E72.0");var subQ14=sQuery(id+"F12.wireOp",EDGE,"E72.1");var subQ16=sQuery(id+"F12.wireOp",EDGE,"E74.1");var subQ18=sQuery(id+"F12.wireOp",EDGE,"E74.8");Q0=qUnion([makeQuery(id+"F12.imprint","IMPRINT",FACE,{"disambiguationData":[TD([[makeQuery(id+"F12.imprint","IMPRINT",EDGE,{"derivedFrom":subQ7}),1.0]])]}),makeQuery(id+"F12.imprint","IMPRINT",FACE,{"disambiguationData":[TD([[makeQuery(id+"F12.imprint","IMPRINT",EDGE,{"derivedFrom":subQ14}),1.0]])]}),makeQuery(id+"F12.imprint","IMPRINT",FACE,{"disambiguationData":[TD([[makeQuery(id+"F12.imprint","IMPRINT",EDGE,{"derivedFrom":subQ16}),1.0]])]}),makeQuery(id+"F12.imprint","IMPRINT",FACE,{"disambiguationData":[TD([[makeQuery(id+"F12.imprint","IMPRINT",EDGE,{"derivedFrom":subQ18}),-1.0]])]})]);}
            var Q1;
            Q1=makeQuery(id+"F5.boolean.opBoolean","SPLIT",FACE,{"disambiguationData":[TD([makeQuery(id+"F5.opExtrude","SWEPT_FACE",FACE,{"disambiguationData":[OSD([sQuery(id+"F4.wireOp",EDGE,"E41")])]})])],"derivedFrom":makeQuery(id+"F3.boolean.opBoolean","COPY",FACE,{"derivedFrom":makeQuery(id+"F3.opExtrude","CAP_FACE",FACE,{"disambiguationData":[OSD([sQuery(id+"F0.wireOp",EDGE,"E25.0"),sQuery(id+"F0.wireOp",EDGE,"E25.1"),sQuery(id+"F0.wireOp",EDGE,"E25.2"),sQuery(id+"F0.wireOp",EDGE,"E25.3"),sQuery(id+"F0.wireOp",EDGE,"E25.4"),sQuery(id+"F0.wireOp",EDGE,"E25.5"),sQuery(id+"F0.wireOp",EDGE,"E25.6"),sQuery(id+"F0.wireOp",EDGE,"E25.7")])],"isStart":false})})});
            extrude(context, id + "F13", {"entities" : qUnion([Q0]), "operationType" : NewBodyOperationType.REMOVE, "endBound" : BoundingType.UP_TO_SURFACE, "endBoundEntityFace" : qUnion([Q1]), "depth" : 25 * mm});
        }
        {
            var Q0;
            Q0=makeQuery(id+"F3.boolean.opBoolean","COPY",EDGE,{"derivedFrom":makeQuery(id+"F3.opExtrude","CAP_EDGE",EDGE,{"disambiguationData":[OSD([sQuery(id+"F0.wireOp",EDGE,"E25.6")])],"isStart":false})});
            var Q1;
            Q1=makeQuery(id+"F8.boolean.opBoolean","INTERSECT",EDGE,{"derivedFrom":[makeQuery(id+"F5.opExtrude","SWEPT_FACE",FACE,{"disambiguationData":[OSD([sQuery(id+"F4.wireOp",EDGE,"E30")])]}),makeQuery(id+"F8.opExtrude","CAP_FACE",FACE,{"disambiguationData":[OSD([sQuery(id+"F7.wireOp",EDGE,"E67")])],"isStart":false})]});
            var Q2;
            Q2=makeQuery(id+"F8.boolean.opBoolean","INTERSECT",EDGE,{"disambiguationData":[OD(1.0)],"derivedFrom":[makeQuery(id+"F5.opExtrude","SWEPT_FACE",FACE,{"disambiguationData":[OSD([sQuery(id+"F4.wireOp",EDGE,"E30")])]}),makeQuery(id+"F8.opExtrude","SWEPT_FACE",FACE,{"disambiguationData":[OSD([sQuery(id+"F7.wireOp",EDGE,"E67")])]})]});
            var Q3;
            {var subQ0=sQuery(id+"F4.wireOp",EDGE,"E30");Q3=makeQuery(id+"F8.boolean.opBoolean","SPLIT",EDGE,{"disambiguationData":[TD([makeQuery(id+"F5.opExtrude","SWEPT_FACE",FACE,{"disambiguationData":[OSD([sQuery(id+"F4.wireOp",EDGE,"E35.filletArc")])]})])],"derivedFrom":makeQuery(id+"F5.opExtrude","CAP_EDGE",EDGE,{"disambiguationData":[OSD([subQ0])],"isStart":false})});}
            var Q4;
            {var subQ0=sQuery(id+"F0.wireOp",EDGE,"E25.7");var subQ1=sQuery(id+"F0.wireOp",EDGE,"E25.1");var subQ2=sQuery(id+"F0.wireOp",EDGE,"E25.6");var subQ3=sQuery(id+"F0.wireOp",EDGE,"E25.5");var subQ4=sQuery(id+"F0.wireOp",EDGE,"E25.4");var subQ5=sQuery(id+"F0.wireOp",EDGE,"E25.0");var subQ6=sQuery(id+"F0.wireOp",EDGE,"E25.2");var subQ7=sQuery(id+"F0.wireOp",EDGE,"E25.3");Q4=makeQuery(id+"F8.boolean.opBoolean","INTERSECT",EDGE,{"derivedFrom":[makeQuery(id+"F5.boolean.opBoolean","SPLIT",FACE,{"disambiguationData":[TD([makeQuery(id+"F2.opExtrude","SWEPT_FACE",FACE,{"disambiguationData":[OSD([subQ5])]})])],"derivedFrom":makeQuery(id+"F3.boolean.opBoolean","COPY",FACE,{"derivedFrom":makeQuery(id+"F3.opExtrude","CAP_FACE",FACE,{"disambiguationData":[OSD([subQ5,subQ1,subQ6,subQ7,subQ4,subQ3,subQ2,subQ0])],"isStart":false})})}),makeQuery(id+"F8.opExtrude","SWEPT_FACE",FACE,{"disambiguationData":[OSD([sQuery(id+"F7.wireOp",EDGE,"E67")])]})]});}
            var Q5;
            Q5=makeQuery(id+"F8.boolean.opBoolean","INTERSECT",EDGE,{"disambiguationData":[OD(0.0)],"derivedFrom":[makeQuery(id+"F5.opExtrude","SWEPT_FACE",FACE,{"disambiguationData":[OSD([sQuery(id+"F4.wireOp",EDGE,"E30")])]}),makeQuery(id+"F8.opExtrude","SWEPT_FACE",FACE,{"disambiguationData":[OSD([sQuery(id+"F7.wireOp",EDGE,"E67")])]})]});
            fillet(context, id + "F14", {"entities" : qUnion([Q0, Q1, Q2, Q3, Q4, Q5]), "radius" : 3 * mm, "tangentPropagation" : true, "allowEdgeOverflow" : false});
        }
        {
            var Q0;
            Q0=makeQuery(id+"F1.opExtrude","CAP_EDGE",EDGE,{"disambiguationData":[OSD([sQuery(id+"F0.wireOp",EDGE,"E1.bottom")])],"isStart":false});
            fillet(context, id + "F15", {"entities" : qUnion([Q0]), "radius" : 2 * mm, "tangentPropagation" : true, "allowEdgeOverflow" : false});
        }
        {
            var Q0;
            {var subQ0=sQuery(id+"F0.wireOp",EDGE,"E21.filletArc");var subQ1=sQuery(id+"F0.wireOp",EDGE,"E7");var subQ2=sQuery(id+"F0.wireOp",EDGE,"E6");var subQ3=sQuery(id+"F0.wireOp",EDGE,"E5");var subQ4=sQuery(id+"F0.wireOp",EDGE,"E4");var subQ5=sQuery(id+"F0.wireOp",EDGE,"E22.filletArc");var subQ6=sQuery(id+"F0.wireOp",EDGE,"E1.bottom");var subQ7=sQuery(id+"F0.wireOp",EDGE,"E1.right");var subQ8=sQuery(id+"F0.wireOp",EDGE,"E1.top");var subQ9=sQuery(id+"F0.wireOp",EDGE,"E1.left");var subQ10=sQuery(id+"F0.wireOp",EDGE,"E23.filletArc");var subQ11=sQuery(id+"F0.wireOp",EDGE,"E24.filletArc");Q0=makeQuery(id+"F2.boolean.opBoolean","SPLIT",FACE,{"disambiguationData":[TD([makeQuery(id+"F1.opExtrude","SWEPT_FACE",FACE,{"disambiguationData":[OSD([subQ6])]})])],"derivedFrom":makeQuery(id+"F1.opExtrude","CAP_FACE",FACE,{"disambiguationData":[OSD([subQ6,subQ8,subQ9,subQ7,subQ4,subQ3,subQ2,subQ1,subQ0,subQ5,subQ10,subQ11])],"isStart":true})});}
            var sketch = newSketch(context, id + "F16", { "sketchPlane" : qUnion([Q0])});
            skSolve(sketch);
        }
        {
            var Q0;
            Q0=makeQuery(id+"F16.imprint","IMPRINT",FACE,{"disambiguationData":[TD([[makeQuery(id+"F16.imprint","IMPRINT",EDGE,{"derivedFrom":makeQuery(id+"F1.opExtrude","CAP_EDGE",EDGE,{"disambiguationData":[OSD([sQuery(id+"F0.wireOp",EDGE,"E1.bottom")])],"isStart":true})}),1.0]])]});
            var sketch = newSketch(context, id + "F17", { "sketchPlane" : qUnion([Q0])});
            skLineSegment(sketch, "E79.0", {"start": v(-64.25, 74.25) * mm, "end": v(64.25, 74.25) * mm});
            skArc(sketch, "E79.1", {"start": v(74.25, 64.25) * mm, "mid": v(71.32, 71.32) * mm, "end": v(64.25, 74.25) * mm});
            skLineSegment(sketch, "E79.2", {"start": v(74.25, -64.25) * mm, "end": v(74.25, 64.25) * mm});
            skLineSegment(sketch, "E79.3", {"start": v(-74.25, -64.25) * mm, "end": v(-74.25, 64.25) * mm});
            skArc(sketch, "E79.4", {"start": v(-74.25, -64.25) * mm, "mid": v(-71.32, -71.32) * mm, "end": v(-64.25, -74.25) * mm});
            skArc(sketch, "E79.5", {"start": v(64.25, -74.25) * mm, "mid": v(71.32, -71.32) * mm, "end": v(74.25, -64.25) * mm});
            skLineSegment(sketch, "E79.6", {"start": v(-64.25, -74.25) * mm, "end": v(64.25, -74.25) * mm});
            skArc(sketch, "E79.7", {"start": v(-64.25, 74.25) * mm, "mid": v(-71.32, 71.32) * mm, "end": v(-74.25, 64.25) * mm});
            skCircle(sketch, "E79.8", {"center": v(60, 60) * mm, "radius": 4 * mm});
            skCircle(sketch, "E79.9", {"center": v(-60, 60) * mm, "radius": 4 * mm});
            skCircle(sketch, "E79.10", {"center": v(-60, -60) * mm, "radius": 4 * mm});
            skCircle(sketch, "E79.11", {"center": v(60, -60) * mm, "radius": 4 * mm});
            skLineSegment(sketch, "E79.12", {"start": v(60, 38.83) * mm, "end": v(60, -38.83) * mm});
            skArc(sketch, "E79.13", {"start": v(54.26, 47.88) * mm, "mid": v(0, 60) * mm, "end": v(-54.26, 47.88) * mm});
            skArc(sketch, "E79.14", {"start": v(60, 38.83) * mm, "mid": v(58.44, 44.2) * mm, "end": v(54.26, 47.88) * mm});
            skArc(sketch, "E79.15", {"start": v(-54.26, 47.88) * mm, "mid": v(-58.44, 44.2) * mm, "end": v(-60, 38.83) * mm});
            skLineSegment(sketch, "E79.16", {"start": v(-60, 38.83) * mm, "end": v(-60, -38.83) * mm});
            skArc(sketch, "E79.17", {"start": v(-60, -38.83) * mm, "mid": v(-58.44, -44.2) * mm, "end": v(-54.26, -47.88) * mm});
            skArc(sketch, "E79.18", {"start": v(-54.26, -47.88) * mm, "mid": v(0, -60) * mm, "end": v(54.26, -47.88) * mm});
            skArc(sketch, "E79.19", {"start": v(54.26, -47.88) * mm, "mid": v(58.44, -44.2) * mm, "end": v(60, -38.83) * mm});
            skSolve(sketch);
        }
        {
            var Q0;
            Q0 = qSketchRegion(id + "F17", true);
            extrude(context, id + "F18", {"entities" : qUnion([Q0]), "depth" : 10 * mm});
        }
    });
